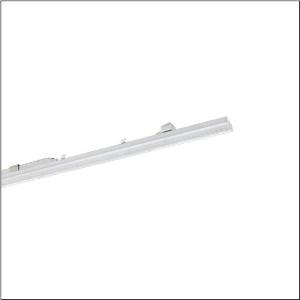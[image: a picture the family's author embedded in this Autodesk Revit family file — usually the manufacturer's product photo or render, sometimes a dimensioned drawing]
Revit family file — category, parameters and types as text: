
# Revit family: tl_l_5wd7a8p0a2b5
name_source: partatom
category: Lighting Fixtures
units: mm (PartAtom-declared; Revit-internal decimal feet)

## family parameters
Cut with Voids When Loaded = No
Host = Face
Light Source = No
Part Type = Normal
Room Calculation Point = No
Round Connector Dimension = Use Diameter
Shared = No

## types (1)
- --- (1 x LED, 5000 lm, 31.5 W, 4000K)
    Apparent Load = 32 VA
    CIE Flux Codes = 49 84 98 100 100
    Color Rendering = 80
    Color Temperature = 4000K
    Default Elevation = 1800 mm
    Description = TL L, luminaire insert, of sheet steel, galvanised, coil coated, white, length: 1.500mm, width: 66mm, height: 67mm, LED light colour: 840, control gear: DALI, with terminal, 5-pole, mains connection: 230..240V, AC, 50/60Hz, rated input power: 63W, primary optical cover: cover, of PMMA, light emission: direct distribution, protection rating (complete): as luminaire, insulation class (complete): insulation class I (protective earthing), certification: CE, impact resistance: IK06, permissible ambient temperature for indoor applications: -35..+35°C, standard: NMF01, packaging unit: 1 piece
    Height = 120 mm
    Lamp = 1 x LED
    Lamp Light Flux = 5000 lm
    Lamp Power = 31.5 W
    Lamp count = 1
    Length = 1690 mm
    Luminous efficacy = 159 lm/W
    Manufacturer = Siteco
    ModVariant = No
    Model = 5WD7A8P0A2B5
    Mounting Place = Ceiling
    Mounting Type = Pendant
    Number of Poles = 1
    OnlyDefault = Yes
    Power Factor = 1
    Product Name = TL L
    Product group = luminaire insert
    ProductGroupID = 901
    Protection Class = Protection class I
    Protection Degree = Degree of protection
    RLX_Detail_Level = 1
    RLX_Emergency_Light_Flux = 0 lm
    RLX_Emergency_Type = 0
    RLX_Emergency_Type_DB = No
    RlxData = <blob elided: 17297 chars, md5=9d245ded>
    Socket = socket
    Standby Power = 0 W
    System Light Flux = 5000 lm
    System Power = 32 W
    Type Comments = factory setting: luminous flux: 100 % | dim-lin: 254 | 646 mA
    Type Image = l_1294382.jpg
    URL = http://relux.com
    VarID = @adj_000695
    Voltage = 0 V
    Weight = 0.00 kg
    Width = 208 mm

## geometry (parser evidence)
native form markers: Blend x4, Sweep x10
no freeform markers — native parametric forms only
